# Revit family: 36-74-116-DN80-100
name_source: partatom
category: Pipe Accessories
units: mm (PartAtom-declared; Revit-internal decimal feet)

## family parameters
Always vertical = No
Cut with Voids When Loaded = No
Part Type = Valve - Breaks Into
Round Connector Dimension = Use Diameter
Shared = No
Work Plane-Based = No

## types (2) — shared parameters
Body_Wallthickness = 5 mm  [stored 0.0164042 ft]
Bonnet_Flange_cut = 7.5 mm  [stored 0.0246063 ft]
Bonnet_Flange_thickness = 15 mm  [stored 0.0492126 ft]
DN 080 = Yes
DN 100 = Yes
DN080 = 36-090-74-34306499
DN100 = 36-110-74-34306499
Description_ = AVK_GATE_VALVE,PE PIPE ENDS
F2 = 34 mm  [stored 0.111549 ft]
Fillet_Thickness = 6 mm  [stored 0.019685 ft]
Name_Height_reference = 10 mm  [stored 0.0328084 ft]
R2f = 15 mm  [stored 0.0492126 ft]
Rib_Height_Reference_1 = 120 mm
Rib_Height_Reference_2 = 110 mm
Rib_Height_Reference_3 = 100 mm
Rib_Thickness = 18 mm  [stored 0.0590551 ft]
Search_table = 36-74-116-DN80-100
URL product pages = https://www.avkvalves.com
zero-valued in all types: Bottom_Reference

## per-type parameters (varying)
- DN 080: At=62.5 mm  [stored 0.205052 ft]; Body_Height=136 mm; Body_Length=180 mm; Body_depth=125 mm; Body_width=72 mm  [stored 0.23622 ft]; Bonnet_Flange_Depth=150 mm; Bonnet_Flange_Width=87 mm; Bonnet_Height=50 mm  [stored 0.164042 ft]; Bonnet_Reference_height=126 mm; Bonnet_Thickness=73.44 mm; Bt=73.44 mm; Bt_2=66 mm  [stored 0.216535 ft]; CL _Thickness=25 mm  [stored 0.082021 ft]; CL_Height_2=67.5 mm  [stored 0.221457 ft]; CL_Thickness 2=25 mm  [stored 0.082021 ft]; Cut_Reference=360 mm; Cut_ref=1350 mm; D=45 mm  [stored 0.147638 ft]; F=8.5 mm  [stored 0.0278871 ft]; F1=10 mm  [stored 0.0328084 ft]; F_OD=60 mm  [stored 0.19685 ft]; Flange_OR=47.5 mm; Flange_Thickness=19 mm  [stored 0.062336 ft]; H=282 mm; H3=342 mm; Horizontal_Flange_width=120 mm; ID=40 mm  [stored 0.131234 ft]; ID (Radius)=40 mm  [stored 0.131234 ft]; L=900 mm; L1=255 mm; L2=390 mm; L_Dia=80 mm  [stored 0.262467 ft]; Length=900 mm; Name_Reference=113.333 mm; Name_Width=36 mm  [stored 0.11811 ft]; Neck_H=44.5 mm  [stored 0.145997 ft]; Neck_T=23 mm  [stored 0.0754593 ft]; Neck_T2=21 mm; Nominal Diameter (DN)=80 mm  [stored 0.262467 ft]; R1tv=1000 mm; Rf=200 mm; Rib_Height_Reference_4=85 mm; Rib_Width_1=36 mm  [stored 0.11811 ft]; Rib_Width_2=36 mm  [stored 0.11811 ft]; Rib_Width_3=36 mm  [stored 0.11811 ft]; Rib_depth_1=36 mm  [stored 0.11811 ft]; Rib_depth_2=36 mm  [stored 0.11811 ft]; Rib_depth_3=36 mm  [stored 0.11811 ft]; Rt=333.333 mm
- DN 100: At=77.5 mm  [stored 0.254265 ft]; Body_Height=148 mm; Body_Length=190 mm; Body_depth=155 mm; Body_width=81 mm  [stored 0.265748 ft]; Bonnet_Flange_Depth=180 mm; Bonnet_Flange_Width=112 mm; Bonnet_Height=55 mm  [stored 0.180446 ft]; Bonnet_Reference_height=138 mm; Bonnet_Thickness=82.62 mm; Bt=82.62 mm; Bt_2=75 mm  [stored 0.246063 ft]; CL _Thickness=29.5 mm  [stored 0.0967848 ft]; CL_Height_2=82.5 mm  [stored 0.270669 ft]; CL_Thickness 2=29.5 mm  [stored 0.0967848 ft]; Cut_Reference=380 mm; Cut_ref=1290 mm; D=55 mm  [stored 0.180446 ft]; F=9.5 mm  [stored 0.031168 ft]; F1=11 mm  [stored 0.0360892 ft]; F_OD=73 mm  [stored 0.239501 ft]; Flange_OR=57.5 mm  [stored 0.188648 ft]; Flange_Thickness=100 mm; H=305 mm; H3=378 mm; Horizontal_Flange_width=146 mm; ID=50 mm  [stored 0.164042 ft]; ID (Radius)=50 mm  [stored 0.164042 ft]; L=860 mm; L1=250 mm; L2=360 mm; L_Dia=100 mm; Length=860 mm; Name_Reference=123.333 mm; Name_Width=40.5 mm  [stored 0.132874 ft]; Neck_H=40.5 mm  [stored 0.132874 ft]; Neck_T=27.5 mm  [stored 0.0902231 ft]; Neck_T2=25.5 mm  [stored 0.0836614 ft]; Nominal Diameter (DN)=100 mm; R1tv=1100 mm; Rf=243.333 mm; Rib_Height_Reference_4=90 mm; Rib_Width_1=40.5 mm  [stored 0.132874 ft]; Rib_Width_2=40.5 mm  [stored 0.132874 ft]; Rib_Width_3=40.5 mm  [stored 0.132874 ft]; Rib_depth_1=40.5 mm  [stored 0.132874 ft]; Rib_depth_2=40.5 mm  [stored 0.132874 ft]; Rib_depth_3=40.5 mm  [stored 0.132874 ft]; Rt=366.667 mm

note: [stored X ft] marks values corroborated as IEEE doubles in the binary element streams (Revit-internal decimal feet)

## geometry (parser evidence)
native form markers: Sweep x2
no freeform markers — native parametric forms only
